# Revit family: BIM_Model_Sanimat_2002_50_HD
name_source: partatom
category: Mechanical Equipment
revit_build: Autodesk Revit 2018 (Build: 20170223_1515(x64)
units: mm (PartAtom-declared; Revit-internal decimal feet)

## family parameters
Always vertical = Yes
Cut with Voids When Loaded = No
Part Type = Normal
Room Calculation Point = No
Round Connector Dimension = Use Radius
Shared = No
Work Plane-Based = No

## types (2) — shared parameters
Cable Length (m) = 4 + 1.5
Capacity (m3/hr) = 55 mm  [stored 0.180446 ft]
Description = Flood-proof double lifting station ideal for effective sewage removal from apartments, large buildings and for both new and renovated structures. It provides automatic sewage pumping from areas below the backwash level in accordance with EN 12050-1.
pumping from areas below the backwash level in accordance with
EN 12050-1.
Discharge Connection = Sleeve 4'' DN 100
Discharge Flange DN 80 = 40 mm  [stored 0.131234 ft]
Head (m) = 19 mm
Inflow DN 100/150 = 50 mm  [stored 0.164042 ft]
Inflow DN 150 = 75 mm  [stored 0.246063 ft]
Inflow DN 150 (Variable with 90° Elbow) = 75 mm  [stored 0.246063 ft]
Inflow/Hand Membrane Pump DN 40 = 20 mm  [stored 0.0656168 ft]
Manufacturer = Sulzer
Model = Lifting Station Type ABS Sanimat 2002
Product Specification Link = http://www.sulzer.com
Rated Voltage (V) = 400 3~
Tank Material = Polyethylene
Vent/Inflow DN 70 = 35 mm  [stored 0.114829 ft]
Weight (Kg) = 132

## per-type parameters (varying)
| type | Impeller | Motor Power (kW) | Motor housing | Rated Current (A) | Rotor Shaft | Speed (r/min) | Volute |
| Sanimat 2002 D/HD | Cast Iron EN-GJL-250 | P1=2.88 P2=2.20 | Cast Iron EN-GJL-250 | 5.2 | Stainless steel 1.4021 (AISI 420) | 1450 | Polyethylene |
| Sanimat 2002 D/XD | <By Category> | P1=3.70 P2=3.00 | <By Category> | 6.2 | <By Category> | 2900 | <By Category> |

note: [stored X ft] marks values corroborated as IEEE doubles in the binary element streams (Revit-internal decimal feet)

## geometry (parser evidence)
native form markers: Sweep x2
no freeform markers — native parametric forms only
